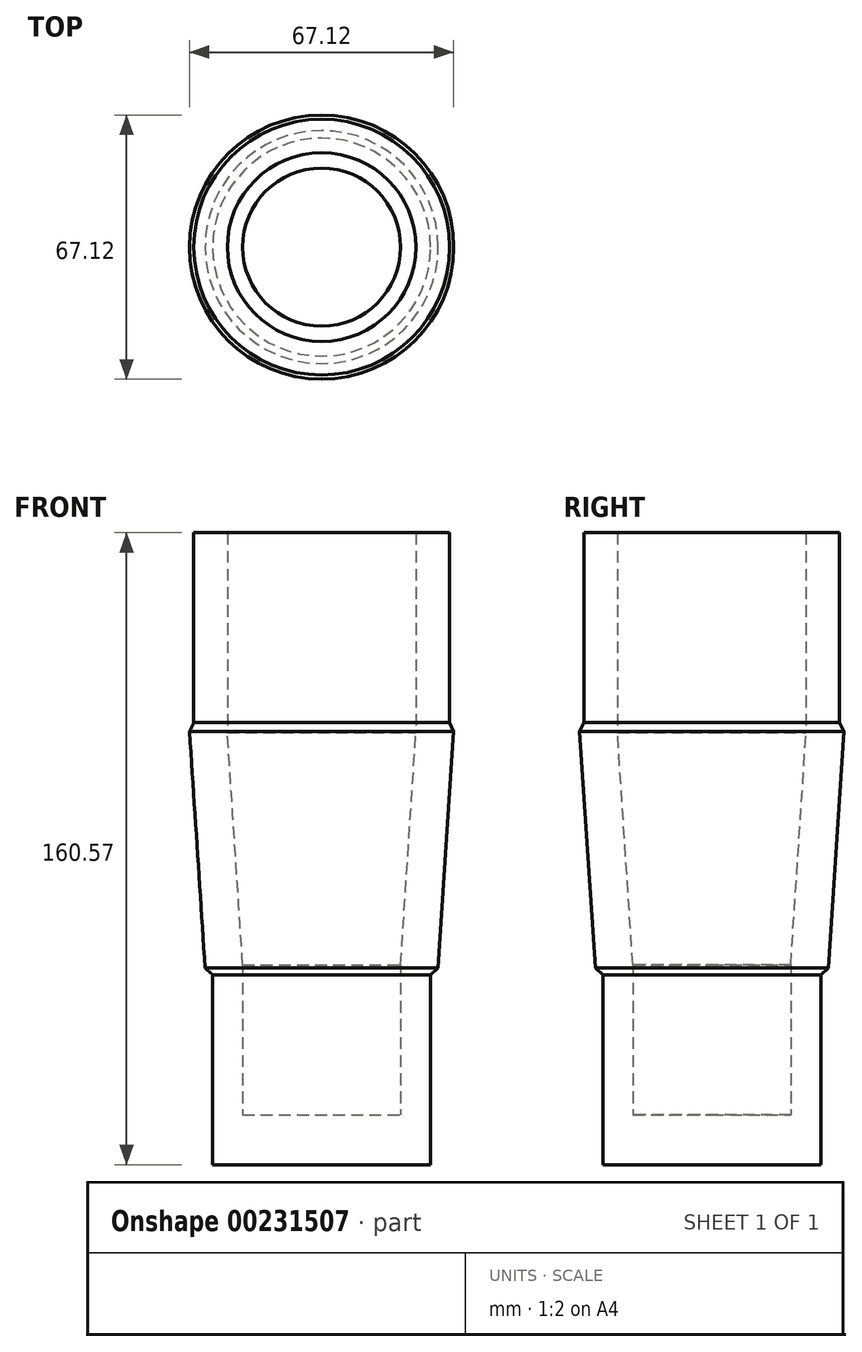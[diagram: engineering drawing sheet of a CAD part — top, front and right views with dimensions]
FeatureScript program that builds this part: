
annotation { "Feature Type Name" : "Feature", "Feature Type Description" : "" }
export const myFeature = defineFeature(function(context is Context, id is Id, definition is map)
    precondition{}
    {
        {
            var Q0;
            Q0=qCreatedBy(makeId("Front.planeOp"),FACE);
            var sketch = newSketch(context, id + "F0", { "sketchPlane" : qUnion([Q0])});
            skLineSegment(sketch, "E0", {"start": v(0, 0) * mm, "end": v(0, 50.43) * mm, "construction": true});
            skLineSegment(sketch, "E1", {"start": v(31.58, 109.77) * mm, "end": v(32.49, 109.77) * mm});
            skLineSegment(sketch, "E2", {"start": v(32.49, 109.77) * mm, "end": v(32.49, 86.9) * mm});
            skLineSegment(sketch, "E3", {"start": v(32.49, 86.9) * mm, "end": v(33.56, 84.6) * mm});
            skLineSegment(sketch, "E4", {"start": v(27.69, 22.86) * mm, "end": v(29.6, 24.53) * mm});
            skLineSegment(sketch, "E5", {"start": v(29.6, 24.53) * mm, "end": v(33.56, 84.6) * mm});
            skLineSegment(sketch, "E6", {"start": v(20.07, 25.4) * mm, "end": v(23.96, 84.37) * mm});
            skLineSegment(sketch, "E7", {"start": v(23.96, 84.37) * mm, "end": v(23.96, 109.77) * mm});
            skLineSegment(sketch, "E8", {"start": v(27.69, 22.86) * mm, "end": v(27.69, 0) * mm});
            skLineSegment(sketch, "E9", {"start": v(20.07, 10.16) * mm, "end": v(20.07, 25.4) * mm});
            skLineSegment(sketch, "E10", {"start": v(0, 10.16) * mm, "end": v(0, 0) * mm});
            skLineSegment(sketch, "E11", {"start": v(27.69, 0) * mm, "end": v(27.69, -25.4) * mm});
            skLineSegment(sketch, "E12", {"start": v(27.69, -25.4) * mm, "end": v(0, -25.4) * mm});
            skLineSegment(sketch, "E13", {"start": v(0, -25.4) * mm, "end": v(0, -12.7) * mm});
            skLineSegment(sketch, "E14", {"start": v(0, -12.7) * mm, "end": v(20.07, -12.7) * mm});
            skLineSegment(sketch, "E15", {"start": v(20.07, -12.7) * mm, "end": v(20.07, 10.16) * mm});
            skLineSegment(sketch, "E16", {"start": v(23.96, 109.77) * mm, "end": v(23.96, 135.17) * mm});
            skLineSegment(sketch, "E17", {"start": v(23.96, 135.17) * mm, "end": v(32.49, 135.17) * mm});
            skLineSegment(sketch, "E18", {"start": v(32.49, 135.17) * mm, "end": v(32.49, 109.77) * mm});
            skSolve(sketch);
        }
        {
            var Q0;
            Q0=qSketchRegion(id+"F0",true);
            var Q1;
            Q1=sQuery(id+"F0.wireOp",EDGE,"E0");
            revolve(context, id + "F1", {"entities" : qUnion([Q0]), "axis" : qUnion([Q1]), "revolveType" : RevolveType.FULL});
        }
    });
